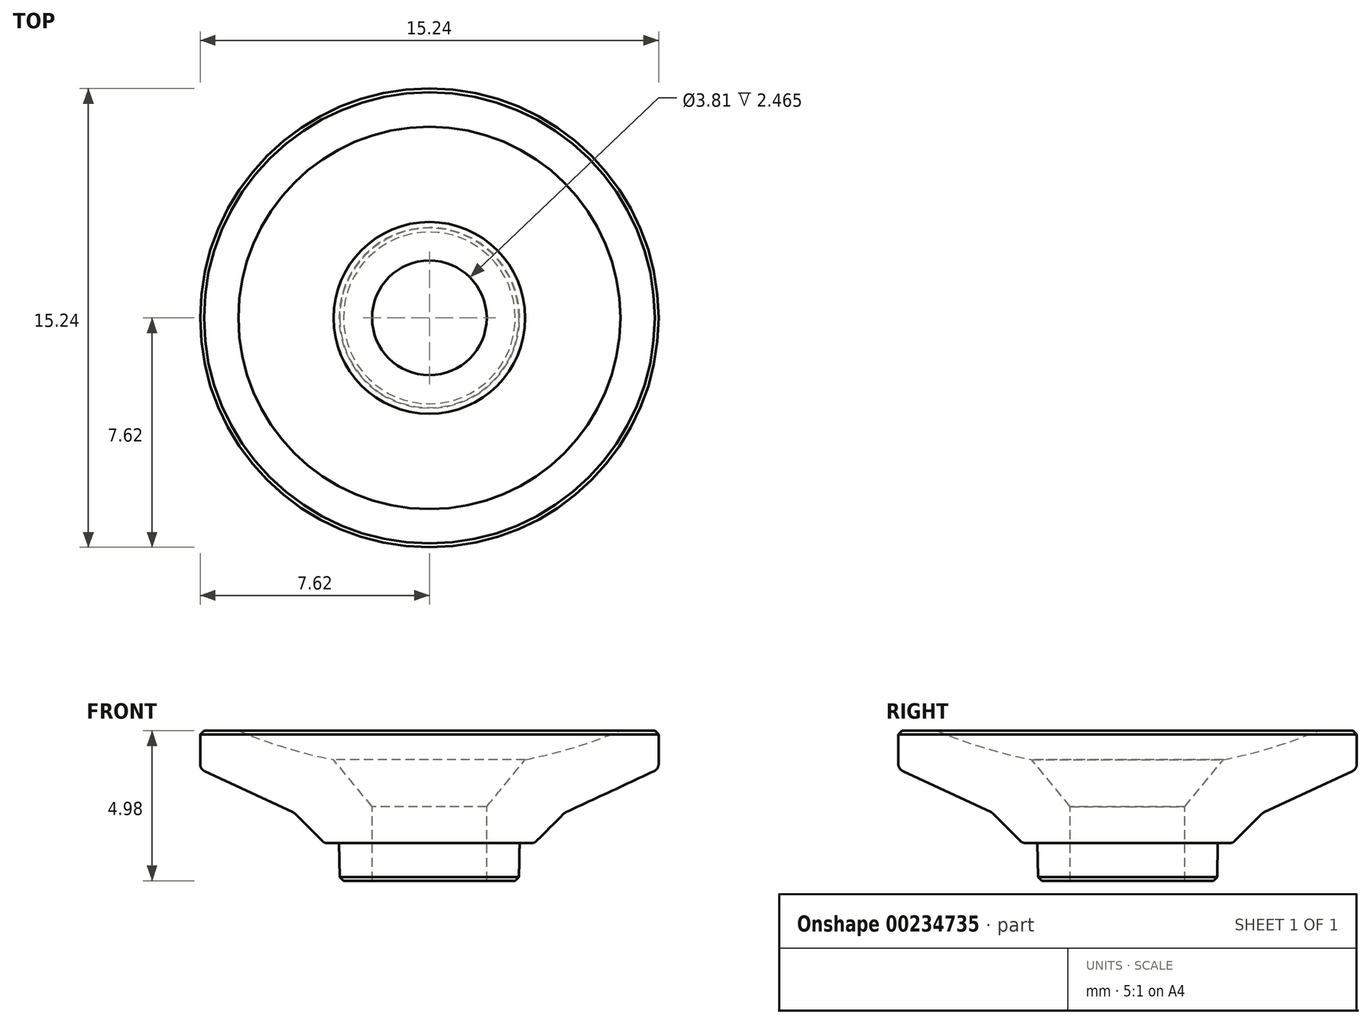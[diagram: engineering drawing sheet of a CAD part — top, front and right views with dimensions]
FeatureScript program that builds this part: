
annotation { "Feature Type Name" : "Feature", "Feature Type Description" : "" }
export const myFeature = defineFeature(function(context is Context, id is Id, definition is map)
    precondition{}
    {
        {
            var Q0;
            Q0=qCreatedBy(makeId("Front.planeOp"),FACE);
            var sketch = newSketch(context, id + "F0", { "sketchPlane" : qUnion([Q0])});
            skLineSegment(sketch, "E0", {"start": v(0, 0) * mm, "end": v(2.98, 0) * mm});
            skLineSegment(sketch, "E1", {"start": v(2.98, 0) * mm, "end": v(3, 1.25) * mm});
            skLineSegment(sketch, "E2", {"start": v(3, 1.25) * mm, "end": v(3.5, 1.25) * mm});
            skLineSegment(sketch, "E3", {"start": v(3.5, 1.25) * mm, "end": v(4.5, 2.26) * mm});
            skLineSegment(sketch, "E4", {"start": v(4.5, 2.26) * mm, "end": v(7.62, 3.71) * mm});
            skLineSegment(sketch, "E5", {"start": v(7.62, 3.71) * mm, "end": v(7.62, 4.98) * mm});
            skLineSegment(sketch, "E6", {"start": v(7.62, 4.98) * mm, "end": v(6.35, 4.98) * mm});
            skLineSegment(sketch, "E7", {"start": v(0, 3.71) * mm, "end": v(0, 0) * mm});
            skArc(sketch, "E8", {"start": v(0, 3.71) * mm, "mid": v(3.24, 4.03) * mm, "end": v(6.35, 4.98) * mm});
            skPoint(sketch, "E9.orphan", {"position": v(0, 4.98) * mm});
            skSolve(sketch);
        }
        {
            var Q0;
            Q0 = qSketchRegion(id + "F0", true);
            var Q1;
            Q1=sQuery(id+"F0.wireOp",EDGE,"E7");
            revolve(context, id + "F1", {"entities" : qUnion([Q0]), "axis" : qUnion([Q1]), "revolveType" : RevolveType.FULL});
        }
        {
            var Q0;
            Q0=makeQuery(id+"F1.opRevolve","SWEPT_EDGE",EDGE,{"disambiguationData":[OSD([sQuery(id+"F0.wireOp",EDGE,"E0"),sQuery(id+"F0.wireOp",EDGE,"E1")])]});
            var Q1;
            Q1=makeQuery(id+"F1.opRevolve","SWEPT_EDGE",EDGE,{"disambiguationData":[OSD([sQuery(id+"F0.wireOp",EDGE,"E5"),sQuery(id+"F0.wireOp",EDGE,"E6")])]});
            chamfer(context, id + "F2", {"entities" : qUnion([Q0, Q1]), "width" : 0.13 * mm, "tangentPropagation" : true});
        }
        {
            var Q0;
            Q0=makeQuery(id+"F1.opRevolve","SWEPT_EDGE",EDGE,{"disambiguationData":[OSD([sQuery(id+"F0.wireOp",EDGE,"KmEllf09-JBKP-2wvp-Ln3d-dT31Av5gxA5O"),sQuery(id+"F0.wireOp",EDGE,"E4")])]});
            var Q1;
            Q1=makeQuery(id+"F1.opRevolve","SWEPT_EDGE",EDGE,{"disambiguationData":[OSD([sQuery(id+"F0.wireOp",EDGE,"E3"),sQuery(id+"F0.wireOp",EDGE,"KmEllf09-JBKP-2wvp-Ln3d-dT31Av5gxA5O")])]});
            var Q2;
            Q2=makeQuery(id+"F1.opRevolve","SWEPT_EDGE",EDGE,{"disambiguationData":[OSD([sQuery(id+"F0.wireOp",EDGE,"E2"),sQuery(id+"F0.wireOp",EDGE,"E3")])]});
            fillet(context, id + "F3", {"entities" : qUnion([Q0, Q1, Q2]), "radius" : 0.25 * mm, "tangentPropagation" : true, "allowEdgeOverflow" : false});
        }
        {
            var Q0;
            Q0=makeQuery(id+"F1.opRevolve","SWEPT_FACE",FACE,{"disambiguationData":[OSD([sQuery(id+"F0.wireOp",EDGE,"E6")])]});
            var sketch = newSketch(context, id + "F4", { "sketchPlane" : qUnion([Q0])});
            skCircle(sketch, "E10", {"center": v(0, 0) * mm, "radius": 1.9 * mm});
            skSolve(sketch);
        }
        {
            var Q0;
            Q0 = qSketchRegion(id + "F4", true);
            extrude(context, id + "F5", {"entities" : qUnion([Q0]), "operationType" : NewBodyOperationType.REMOVE, "endBound" : BoundingType.THROUGH_ALL, "oppositeDirection" : true, "depth" : 25.4 * mm});
        }
        {
            var Q0;
            Q0=makeQuery(id+"F5.boolean.opBoolean","COPY",EDGE,{"derivedFrom":makeQuery(id+"F5.opExtrude","CAP_EDGE",EDGE,{"disambiguationData":[OSD([sQuery(id+"F4.wireOp",EDGE,"E10")])],"isStart":true})});
            var Q1;
            Q1=makeQuery(id+"F5.boolean.opBoolean","INTERSECT",EDGE,{"derivedFrom":[makeQuery(id+"F1.opRevolve","SWEPT_FACE",FACE,{"disambiguationData":[OSD([sQuery(id+"F0.wireOp",EDGE,"E8")])]}),makeQuery(id+"F5.opExtrude","SWEPT_FACE",FACE,{"disambiguationData":[OSD([sQuery(id+"F4.wireOp",EDGE,"E10")])]})]});
            chamfer(context, id + "F6", {"entities" : qUnion([Q0, Q1]), "width" : 1.59 * mm, "tangentPropagation" : true});
        }
    });
